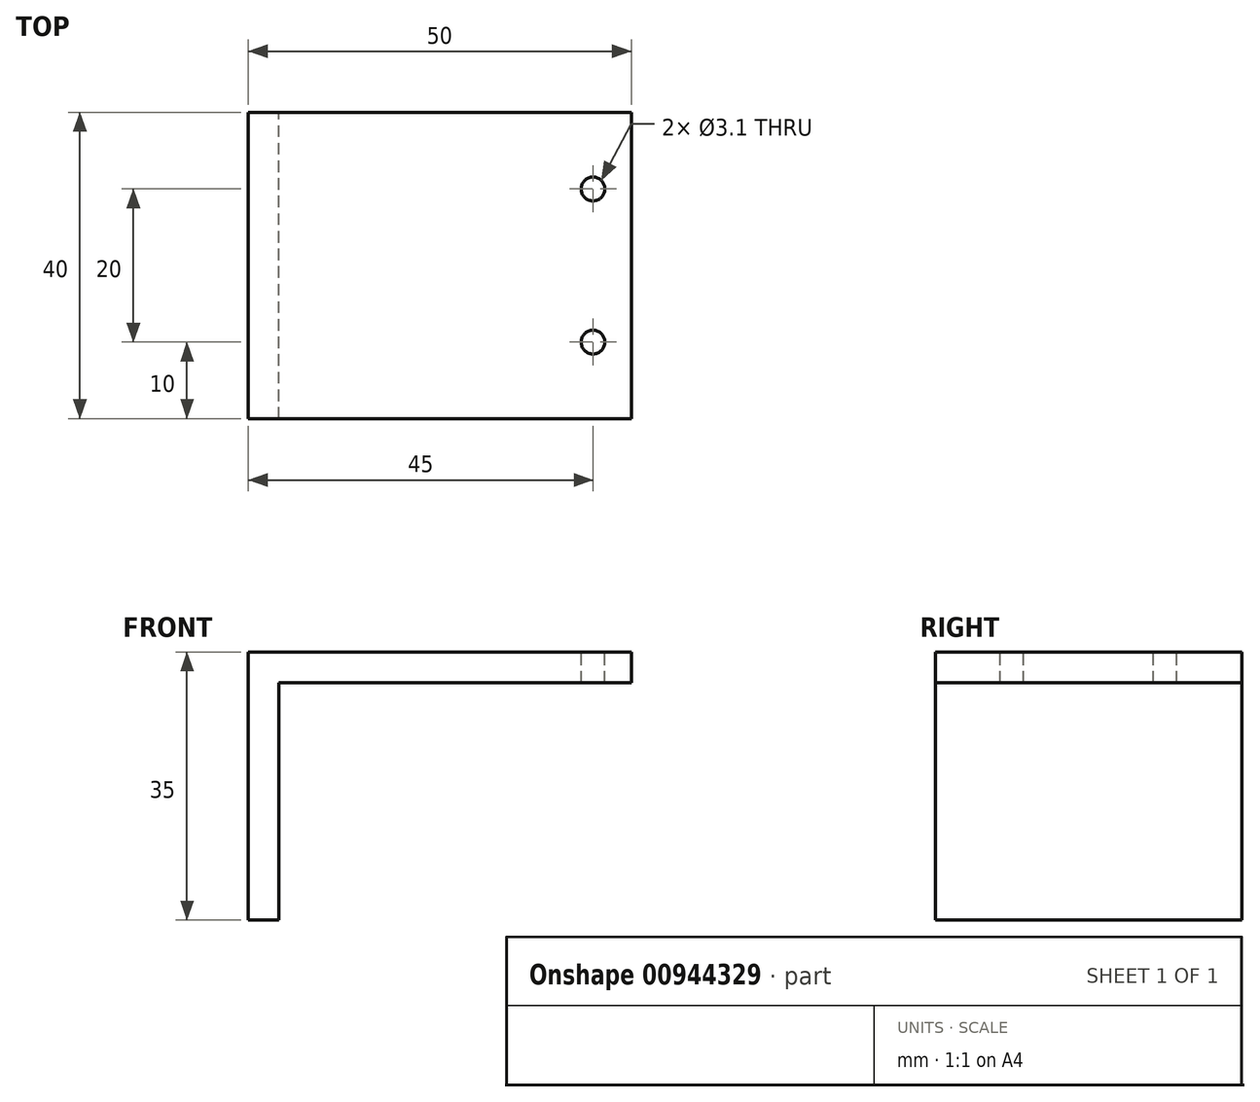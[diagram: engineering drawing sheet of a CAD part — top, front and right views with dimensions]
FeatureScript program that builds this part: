
annotation { "Feature Type Name" : "Feature", "Feature Type Description" : "" }
export const myFeature = defineFeature(function(context is Context, id is Id, definition is map)
    precondition{}
    {
        {
            var Q0;
            Q0=qCreatedBy(makeId("Front.planeOp"),FACE);
            var sketch = newSketch(context, id + "F0", { "sketchPlane" : qUnion([Q0])});
            skLineSegment(sketch, "E0", {"start": v(0, 0) * mm, "end": v(0, -35) * mm});
            skLineSegment(sketch, "E1", {"start": v(0, -35) * mm, "end": v(4, -35) * mm});
            skLineSegment(sketch, "E2", {"start": v(4, -35) * mm, "end": v(4, -4) * mm});
            skLineSegment(sketch, "E3", {"start": v(4, -4) * mm, "end": v(50, -4) * mm});
            skLineSegment(sketch, "E4", {"start": v(50, -4) * mm, "end": v(50, 0) * mm});
            skLineSegment(sketch, "E5", {"start": v(50, 0) * mm, "end": v(0, 0) * mm});
            skSolve(sketch);
        }
        {
            var Q0;
            Q0=makeQuery(id+"F0.imprint","IMPRINT",FACE,{"disambiguationData":[TD([[makeQuery(id+"F0.imprint","IMPRINT",EDGE,{"derivedFrom":sQuery(id+"F0.wireOp",EDGE,"E0")}),1.0]])]});
            extrude(context, id + "F1", {"entities" : qUnion([Q0]), "depth" : 40 * mm, "offsetDistance" : 25 * mm});
        }
        {
            var Q0;
            Q0=makeQuery(id+"F1.opExtrude","SWEPT_FACE",FACE,{"disambiguationData":[OSD([sQuery(id+"F0.wireOp",EDGE,"E5")])]});
            var sketch = newSketch(context, id + "F2", { "sketchPlane" : qUnion([Q0])});
            skLineSegment(sketch, "E6", {"start": v(0, -20) * mm, "end": v(50, -20) * mm, "construction": true});
            skCircle(sketch, "E7.MirrorC", {"center": v(45, -10) * mm, "radius": 1.55 * mm});
            skCircle(sketch, "E8.MirrorC", {"center": v(45, -30) * mm, "radius": 1.55 * mm});
            skLineSegment(sketch, "E9", {"start": v(45, -40) * mm, "end": v(45, 0) * mm, "construction": true});
            skSolve(sketch);
        }
        {
            var Q0;
            Q0=qSketchRegion(id+"F2",true);
            extrude(context, id + "F3", {"entities" : qUnion([Q0]), "operationType" : NewBodyOperationType.REMOVE, "endBound" : BoundingType.UP_TO_NEXT, "oppositeDirection" : true, "depth" : 25 * mm, "offsetDistance" : 25 * mm});
        }
    });
